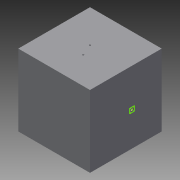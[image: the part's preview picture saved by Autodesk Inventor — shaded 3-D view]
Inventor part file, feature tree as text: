
AUTODESK INVENTOR PART (.ipt)
format: ipt  version: 2014 (Build 180170000, 170)  size: 267,264 bytes
history: native  units: mm
features: other x49, sketch x4, extrude x1
ambient origin geometry x8: Origin, YZ Plane, XZ Plane, XY Plane, X Axis, Y Axis, Z Axis, Center Point
bodies: 实体1 (feature_tree)
feature tree (54):
  extrude  "拉伸1"  TaperAngle=0.0deg  [1 undecoded]
  other  "UCS1"
  other  "UCS2"
  other  "UCS3"
  other  "UCS4"
  other  "UCS5"
  other  "UCS6"
  other  "Footprint1"
  sketch  "草图1"  dims[d0=1000.0mm d1=0.0mm]
  other  "UCS1: YZ 平面"
  other  "UCS1: XZ 平面"
  other  "UCS1: XY 平面"
  other  "UCS1: X 轴"
  other  "UCS1: Y 轴"
  other  "UCS1: Z 轴"
  other  "UCS1: 原点"
  other  "UCS2: YZ 平面"
  other  "UCS2: XZ 平面"
  other  "UCS2: XY 平面"
  other  "UCS2: X 轴"
  other  "UCS2: Y 轴"
  other  "UCS2: Z 轴"
  other  "UCS2: 原点"
  other  "UCS3: YZ 平面"
  other  "UCS3: XZ 平面"
  other  "UCS3: XY 平面"
  other  "UCS3: X 轴"
  other  "UCS3: Y 轴"
  other  "UCS3: Z 轴"
  other  "UCS3: 原点"
  other  "UCS4: YZ 平面"
  other  "UCS4: XZ 平面"
  other  "UCS4: XY 平面"
  other  "UCS4: X 轴"
  other  "UCS4: Y 轴"
  other  "UCS4: Z 轴"
  other  "UCS4: 原点"
  other  "UCS5: YZ 平面"
  other  "UCS5: XZ 平面"
  other  "UCS5: XY 平面"
  other  "UCS5: X 轴"
  other  "UCS5: Y 轴"
  other  "UCS5: Z 轴"
  other  "UCS5: 原点"
  other  "UCS6: YZ 平面"
  other  "UCS6: XZ 平面"
  other  "UCS6: XY 平面"
  other  "UCS6: X 轴"
  other  "UCS6: Y 轴"
  other  "UCS6: Z 轴"
  other  "UCS6: 原点"
  sketch  "草图2"  dims[d2=0.0mm d3=0.0mm d4=0.0mm d5=0.0mm d6=0.0mm d7=0.0mm]
  sketch  "草图3"  dims[d8=0.0mm d9=0.0mm d10=0.0mm d11=0.0mm d12=0.0mm d13=0.0mm]
  sketch  "草图6"  dims[d14=0.0mm d15=0.0mm d16=0.0mm d17=0.0mm d18=0.0mm d19=0.0mm d20=0.0mm d21=0.0mm d22=0.0mm d23=0.0mm d24=0.0mm d25=0.0mm d26=0.0mm d27=0.0mm d28=0.0mm d29=0.0mm d30=0.0mm d31=0.0mm d32=0.0mm d33=0.0mm d34=0.0mm d35=0.0mm d36=0.0mm d37=0.0mm d38=0.0mm d42=-17.0mm d43=0.0mm d44=0.0mm d48=0.0mm d54=0.0mm]
note: 1 required parameter value undecoded (feature->parameter linkage not recoverable at this tier; creation-order binding heuristic only, values carry confidence <= 0.55)
